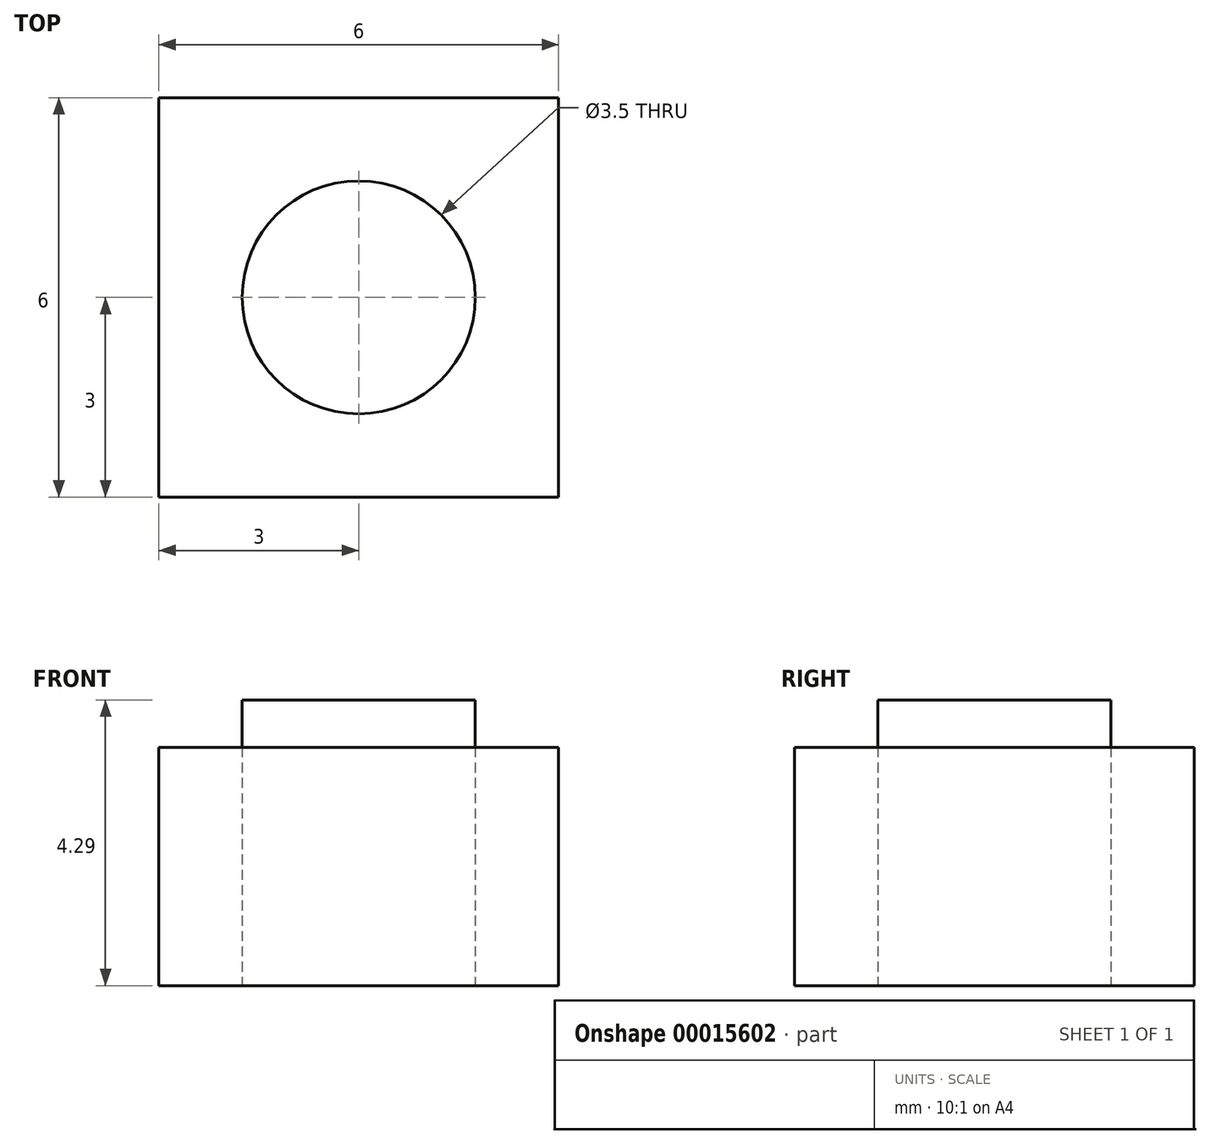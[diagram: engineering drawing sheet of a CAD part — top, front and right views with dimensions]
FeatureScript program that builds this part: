
annotation { "Feature Type Name" : "Feature", "Feature Type Description" : "" }
export const myFeature = defineFeature(function(context is Context, id is Id, definition is map)
    precondition{}
    {
        {
            var Q0;
            Q0=qCreatedBy(makeId("Top.planeOp"),FACE);
            var sketch = newSketch(context, id + "F0", { "sketchPlane" : qUnion([Q0])});
            skLineSegment(sketch, "E0.rect.bottom", {"start": v(3, 3) * mm, "end": v(-3, 3) * mm});
            skLineSegment(sketch, "E0.rect.top", {"start": v(3, -3) * mm, "end": v(-3, -3) * mm});
            skLineSegment(sketch, "E0.rect.left", {"start": v(3, 3) * mm, "end": v(3, -3) * mm});
            skLineSegment(sketch, "E0.rect.right", {"start": v(-3, 3) * mm, "end": v(-3, -3) * mm});
            skPoint(sketch, "E0.rect.middle", {"position": v(0, 0) * mm});
            skCircle(sketch, "E1", {"center": v(0, 0) * mm, "radius": 1.75 * mm});
            skSolve(sketch);
        }
        {
            var Q0;
            Q0=makeQuery(id+"F0.imprint","IMPRINT",FACE,{"disambiguationData":[TD([[makeQuery(id+"F0.imprint","IMPRINT",EDGE,{"derivedFrom":sQuery(id+"F0.wireOp",EDGE,"E0.rect.bottom")}),1.0]])]});
            extrude(context, id + "F1", {"entities" : qUnion([Q0]), "depth" : 3.58 * mm});
        }
        {
            var Q0;
            Q0=qCreatedBy(makeId("Top.planeOp"),FACE);
            var sketch = newSketch(context, id + "F2", { "sketchPlane" : qUnion([Q0])});
            skCircle(sketch, "E2", {"center": v(0, 0) * mm, "radius": 1.75 * mm});
            skSolve(sketch);
        }
        {
            var Q0;
            Q0=makeQuery(id+"F2.imprint","IMPRINT",FACE,{"disambiguationData":[TD([[makeQuery(id+"F2.imprint","IMPRINT",EDGE,{"derivedFrom":sQuery(id+"F2.wireOp",EDGE,"E2")}),1.0]])]});
            extrude(context, id + "F3", {"entities" : qUnion([Q0]), "depth" : 4.3 * mm});
        }
    });
